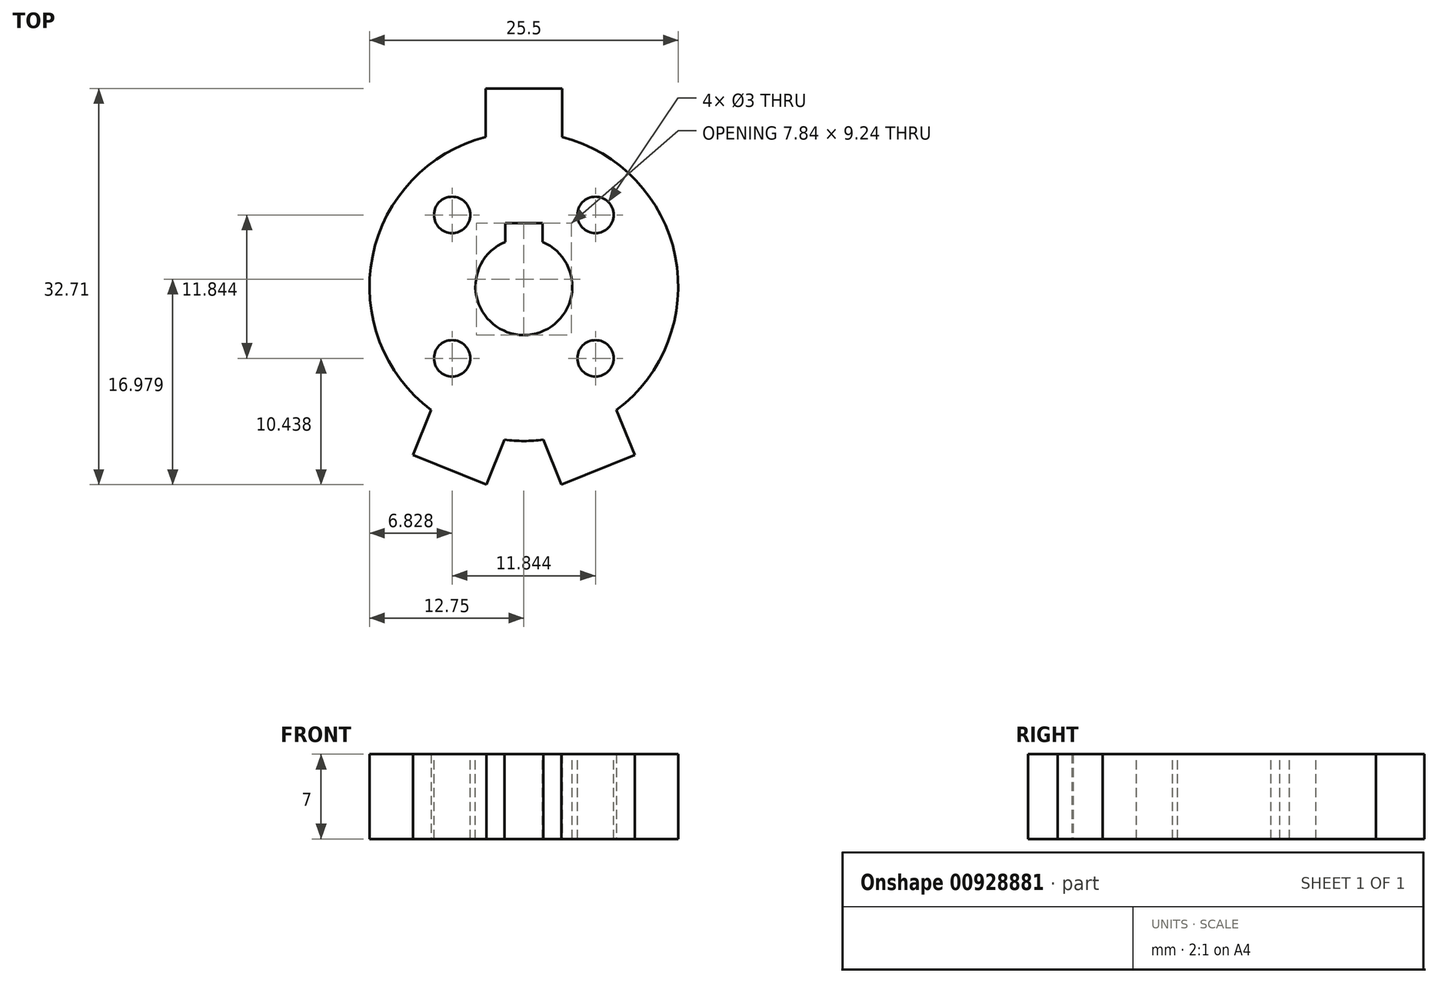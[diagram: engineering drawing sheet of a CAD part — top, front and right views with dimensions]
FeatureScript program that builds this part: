
annotation { "Feature Type Name" : "Feature", "Feature Type Description" : "" }
export const myFeature = defineFeature(function(context is Context, id is Id, definition is map)
    precondition{}
    {
        {
            var Q0;
            Q0=qCreatedBy(makeId("Top.planeOp"),FACE);
            var sketch = newSketch(context, id + "F0", { "sketchPlane" : qUnion([Q0])});
            skArc(sketch, "E0", {"start": v(7.65, -10.2) * mm, "mid": v(12.5, 2.5) * mm, "end": v(3.15, 12.35) * mm});
            skLineSegment(sketch, "E1", {"start": v(0, 12.75) * mm, "end": v(0, -12.75) * mm, "construction": true});
            skLineSegment(sketch, "E2", {"start": v(-3.15, 16.35) * mm, "end": v(0, 16.35) * mm});
            skLineSegment(sketch, "E3", {"start": v(0, 16.35) * mm, "end": v(3.15, 16.35) * mm});
            skLineSegment(sketch, "E4", {"start": v(-3.15, 16.35) * mm, "end": v(-3.15, 12.35) * mm});
            skLineSegment(sketch, "E5", {"start": v(3.15, 16.35) * mm, "end": v(3.15, 12.35) * mm});
            skLineSegment(sketch, "E6", {"start": v(1.6, -12.65) * mm, "end": v(7.65, -10.2) * mm, "construction": true});
            skLineSegment(sketch, "E7", {"start": v(1.6, -12.65) * mm, "end": v(3.1, -16.36) * mm});
            skLineSegment(sketch, "E8", {"start": v(7.65, -10.2) * mm, "end": v(9.15, -13.9) * mm});
            skLineSegment(sketch, "E9", {"start": v(3.1, -16.36) * mm, "end": v(9.15, -13.9) * mm});
            skLineSegment(sketch, "E10.MirrorCS", {"start": v(-1.6, -12.65) * mm, "end": v(-3.1, -16.36) * mm});
            skLineSegment(sketch, "E11.MirrorCS", {"start": v(-3.1, -16.36) * mm, "end": v(-9.15, -13.9) * mm});
            skLineSegment(sketch, "E12.MirrorCS", {"start": v(-7.65, -10.2) * mm, "end": v(-9.15, -13.9) * mm});
            skArc(sketch, "E13.trimOffspring", {"start": v(-1.6, -12.65) * mm, "mid": v(0, -12.75) * mm, "end": v(1.6, -12.65) * mm});
            skArc(sketch, "E14.trimOffspring", {"start": v(-3.15, 12.35) * mm, "mid": v(-12.5, 2.5) * mm, "end": v(-7.65, -10.2) * mm});
            skLineSegment(sketch, "E15", {"start": v(-1.6, -12.65) * mm, "end": v(1.6, -12.65) * mm, "construction": true});
            skLineSegment(sketch, "E16", {"start": v(-3.1, -16.36) * mm, "end": v(3.1, -16.36) * mm, "construction": true});
            skLineSegment(sketch, "E17", {"start": v(-9.15, -13.9) * mm, "end": v(9.15, -13.9) * mm, "construction": true});
            skLineSegment(sketch, "E18", {"start": v(-7.65, -10.2) * mm, "end": v(7.65, -10.2) * mm, "construction": true});
            skSolve(sketch);
        }
        {
            var Q0;
            Q0=qSketchRegion(id+"F0",true);
            extrude(context, id + "F1", {"entities" : qUnion([Q0]), "depth" : 7 * mm, "offsetDistance" : 25 * mm});
        }
        {
            var Q0;
            Q0=makeQuery(id+"F1.opExtrude","CAP_FACE",FACE,{"disambiguationData":[OSD([sQuery(id+"F0.wireOp",EDGE,"E0"),sQuery(id+"F0.wireOp",EDGE,"E2"),sQuery(id+"F0.wireOp",EDGE,"E3"),sQuery(id+"F0.wireOp",EDGE,"E4"),sQuery(id+"F0.wireOp",EDGE,"E5"),sQuery(id+"F0.wireOp",EDGE,"E7"),sQuery(id+"F0.wireOp",EDGE,"E8"),sQuery(id+"F0.wireOp",EDGE,"E9"),sQuery(id+"F0.wireOp",EDGE,"E10.MirrorCS"),sQuery(id+"F0.wireOp",EDGE,"E11.MirrorCS"),sQuery(id+"F0.wireOp",EDGE,"E12.MirrorCS"),sQuery(id+"F0.wireOp",EDGE,"E13.trimOffspring"),sQuery(id+"F0.wireOp",EDGE,"E14.trimOffspring")])],"isStart":false});
            var sketch = newSketch(context, id + "F2", { "sketchPlane" : qUnion([Q0])});
            skArc(sketch, "E19", {"start": v(-1.55, 3.69) * mm, "mid": v(0, -4) * mm, "end": v(1.55, 3.69) * mm});
            skLineSegment(sketch, "E20", {"start": v(0, 4) * mm, "end": v(0, 5.24) * mm, "construction": true});
            skLineSegment(sketch, "E21", {"start": v(0, 5.24) * mm, "end": v(1.55, 5.24) * mm});
            skLineSegment(sketch, "E22", {"start": v(0, 5.24) * mm, "end": v(-1.55, 5.24) * mm});
            skLineSegment(sketch, "E23", {"start": v(1.55, 5.24) * mm, "end": v(1.55, 3.69) * mm});
            skLineSegment(sketch, "E24", {"start": v(-1.55, 5.24) * mm, "end": v(-1.55, 3.69) * mm});
            skLineSegment(sketch, "E25", {"start": v(-12.75, 0) * mm, "end": v(0, 0) * mm, "construction": true});
            skLineSegment(sketch, "E26", {"start": v(0, 0) * mm, "end": v(-2.83, 2.83) * mm, "construction": true});
            skLineSegment(sketch, "E27", {"start": v(0, 0) * mm, "end": v(8.84, -8.84) * mm, "construction": true});
            skLineSegment(sketch, "E28.MirrorCS", {"start": v(0, 0) * mm, "end": v(8.84, 8.84) * mm, "construction": true});
            skLineSegment(sketch, "E29.MirrorCS", {"start": v(0, 0) * mm, "end": v(-9.02, -9.02) * mm, "construction": true});
            skCircle(sketch, "E30", {"center": v(-5.92, 5.92) * mm, "radius": 1.5 * mm});
            skCircle(sketch, "E31.1.0", {"center": v(-5.92, -5.92) * mm, "radius": 1.5 * mm});
            skCircle(sketch, "E31.2.0", {"center": v(5.92, -5.92) * mm, "radius": 1.5 * mm});
            skCircle(sketch, "E31.3.0", {"center": v(5.92, 5.92) * mm, "radius": 1.5 * mm});
            skLineSegment(sketch, "E32", {"start": v(-2.83, 2.83) * mm, "end": v(-9.02, 9.02) * mm, "construction": true});
            skSolve(sketch);
        }
        {
            var Q0;
            Q0=qSketchRegion(id+"F2",true);
            var Q1;
            Q1=makeQuery(id+"F1.opExtrude","CAP_FACE",FACE,{"disambiguationData":[OSD([sQuery(id+"F0.wireOp",EDGE,"E0"),sQuery(id+"F0.wireOp",EDGE,"E2"),sQuery(id+"F0.wireOp",EDGE,"E3"),sQuery(id+"F0.wireOp",EDGE,"E4"),sQuery(id+"F0.wireOp",EDGE,"E5"),sQuery(id+"F0.wireOp",EDGE,"E7"),sQuery(id+"F0.wireOp",EDGE,"E8"),sQuery(id+"F0.wireOp",EDGE,"E9"),sQuery(id+"F0.wireOp",EDGE,"E10.MirrorCS"),sQuery(id+"F0.wireOp",EDGE,"E11.MirrorCS"),sQuery(id+"F0.wireOp",EDGE,"E12.MirrorCS"),sQuery(id+"F0.wireOp",EDGE,"E13.trimOffspring"),sQuery(id+"F0.wireOp",EDGE,"E14.trimOffspring")])],"isStart":true});
            extrude(context, id + "F3", {"entities" : qUnion([Q0]), "operationType" : NewBodyOperationType.REMOVE, "endBound" : BoundingType.UP_TO_SURFACE, "oppositeDirection" : true, "depth" : 25 * mm, "endBoundEntityFace" : qUnion([Q1]), "offsetDistance" : 25 * mm});
        }
    });
